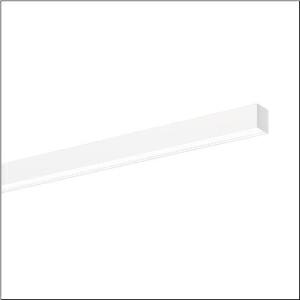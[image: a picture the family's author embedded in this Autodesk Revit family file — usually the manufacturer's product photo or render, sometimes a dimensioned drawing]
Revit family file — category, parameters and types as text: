
# Revit family: silica_r__21_51mx20tbt2w_71dc
name_source: partatom
category: Lighting Fixtures
units: mm (PartAtom-declared; Revit-internal decimal feet)

## family parameters
Cut with Voids When Loaded = No
Host = Face
Light Source = No
Part Type = Normal
Room Calculation Point = No
Round Connector Dimension = Use Diameter
Shared = No

## types (1)
- --- (1 x LED, 3000 lm, 25.6 W, 6500K)
    Apparent Load = 26 VA
    CIE Flux Codes = 48 79 96 100 100
    Color Rendering = 80
    Color Temperature = 6500K
    Default Elevation = 1800 mm
    Description = Silica® 21, office luminaire, primary optical cover: cover, of PMMA, opal, light emission: direct distribution, primary light characteristic: symmetric, installation type: surface-mounted, LED, rated luminous flux: 3.000lm, luminous efficacy: 112lm/W, light colour: 8tw, colour temperature: 2700..6500K, control gear: ECG DALI, with terminal, 3+2-pole, max. 2.5mm², mains connection: 220..240V, AC, 50/60Hz, rated input power: 26.9W, luminaire housing, of aluminium, traffic white (RAL 9016), length: 1.504mm, width: 53mm, height: 53mm, protection rating (complete): IP20, insulation class (complete): insulation class I (protective earthing), certification: CE, permissible operating ambient temperature: 0..+35°C, standard: EN 50419, packaging unit: 1 piece
    Height = 0 mm  [stored 0 ft]
    Lamp = 1 x LED
    Lamp Light Flux = 3000 lm
    Lamp Power = 25.6 W
    Lamp count = 1
    Length = 1504 mm
    Luminous efficacy = 117 lm/W
    Manufacturer = Siteco
    ModVariant = No
    Model = 51MX20TBT2W
    Mounting Place = Ceiling
    Mounting Type = Recessed
    Number of Poles = 1
    OnlyDefault = Yes
    Power Factor = 1
    Product Name = Silica® 21
    Product group = office luminaire | ceiling recessed
    ProductGroupID = 401
    Protection Class = Protection class I
    Protection Degree = IP 20
    RLX_Detail_Level = 1
    RLX_Emergency_Light_Flux = 0 lm
    RLX_Emergency_Type = 0
    RLX_Emergency_Type_DB = No
    RlxData = <blob elided: 20789 chars, md5=2868487a>
    Socket = socket
    Standby Power = 0 W
    System Light Flux = 3000 lm
    System Power = 26 W
    Type Comments = individual setting
    Type Image = l_1297777.jpg
    URL = http://relux.com
    VarID = @adj_071029
    Voltage = 0 V
    Weight = 0.00 kg
    Width = 53 mm

note: [stored X ft] marks values corroborated as IEEE doubles in the binary element streams (Revit-internal decimal feet)

## geometry (parser evidence)
native form markers: Blend x4, Sweep x11
no freeform markers — native parametric forms only
